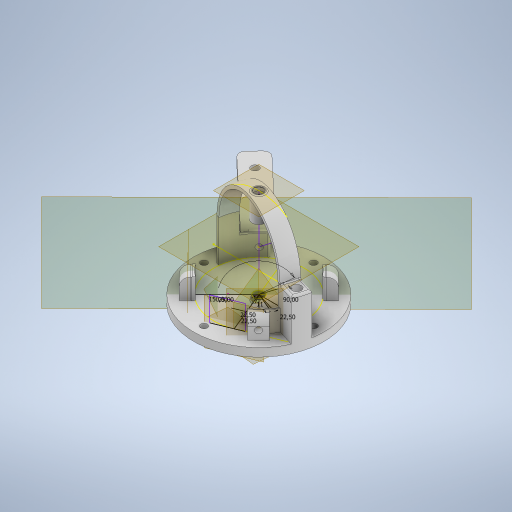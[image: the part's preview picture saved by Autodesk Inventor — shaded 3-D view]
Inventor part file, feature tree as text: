
AUTODESK INVENTOR PART (.ipt)
format: ipt  version: 2024 (Build 280153000, 153)  size: 738,816 bytes
history: native  units: in
note: dims shown in document units (in); Inventor stores cm internally (conversion verified against a paired STEP export)
features: sketch x38, extrude x19, plane x10, fillet x6, revolve x1, chamfer x1, pattern_circular x1
ambient origin geometry x8: Origin, YZ Plane, XZ Plane, XY Plane, X Axis, Y Axis, Z Axis, Center Point
bodies: Solid1 (feature_tree)
feature tree (76):
  extrude  "Plate"  Depth=0.1575in TaperAngle=0.0deg
  sketch  "Sketch4"  dims[d12=0.1969in d13=0.1299in]
  extrude  "Screw holes"  Depth=0.1299in
  extrude  "Optical hole"  Depth=0.1575in TaperAngle=0.0deg
  extrude  "Extrusion8"  Depth=0.1575in TaperAngle=0.0deg
  extrude  "Extrusion9"  Depth=0.3937in
  fillet  "Fillet1"  Radius=0.3937in
  sketch  "Sketch13"  dims[d60=0.1142in d61=7.874in d62=0.0in]
  plane  "Work Plane1"
  sketch  "Sketch15"  dims[d66=0.2362in d67=0.4724in]
  plane  "Work Plane2"
  extrude  "Extrusion12"  Depth=0.0394in
  extrude  "Extrusion13"  Depth=0.3937in TaperAngle=0.0deg
  fillet  "Fillet2"  Radius=0.0591in
  sketch  "Sketch29"  dims[d111=30.0deg]
  plane  "Work Plane5"
  sketch  "Sketch32"  dims[d120=0.3214in]
  plane  "Work Plane6"
  sketch  "Sketch36"  dims[d121=0.1732in d122=0.1181in d123=0.0in]
  sketch  "Sketch37"  dims[d124=0.1969in d125=0.0in d127=0.1575in]
  extrude  "Extrusion22"  Depth=7.874in TaperAngle=0.0deg
  extrude  "Extrusion23"  Depth=5.9055in TaperAngle=0.0deg
  extrude  "Extrusion24"  Depth=0.4724in
  sketch  "Sketch40"  dims[d134=0.7874in d135=90.0deg d136=0.1693in]
  sketch  "Sketch41"  dims[d137=0.2559in d138=0.3937in d139=0.0in]
  plane  "Work Plane7"
  sketch  "Sketch42"  dims[d140=0.2559in d141=0.1811in]
  revolve  "Revolution3"  [1 undecoded]
  sketch  "Sketch43"  dims[d142=0.4724in d143=0.0in d144=0.0394in d145=0.0394in]
  sketch  "Sketch44"  dims[d146=0.0197in d147=0.0787in d148=45.0deg d149=0.1181in d150=0.0394in d151=0.0in d152=0.0in]
  plane  "Work Plane8"
  extrude  "Extrusion25"  Depth=0.3937in
  extrude  "Extrusion26"  Depth=0.1575in
  fillet  "Fillet6"  Radius=1.7323in
  fillet  "Fillet7"  [1 undecoded]
  chamfer  "Chamfer1"  Distance=0.1181in
  extrude  "Extrusion27"  Depth=0.1575in
  pattern_circular  "Circular Pattern1"  Count=2  [1 undecoded]
  extrude  "Extrusion11"  TaperAngle=90.0deg  [1 undecoded]
  extrude  "Extrusion10"  TaperAngle=90.0deg  [1 undecoded]
  fillet  "Fillet8"  Radius=0.1693in
  sketch  "Sketch48"  dims[d158=22.5deg]
  sketch  "Sketch50"  dims[d159=0.4331in]
  sketch  "Sketch51"  dims[d162=22.5deg]
  plane  "Work Plane10"
  sketch  "Sketch52"  dims[d163=22.5deg]
  sketch  "Sketch55"  dims[d164=0.1772in]
  plane  "Work Plane12"
  sketch  "Sketch56"  dims[d165=0.7087in d166=0.0in]
  plane  "Work Plane13"
  extrude  "Extrusion28"  Depth=0.3937in TaperAngle=0.0deg
  plane  "Work Plane14"
  sketch  "Sketch58"  dims[d169=0.3937in d170=0.0in]
  extrude  "Extrusion29"  Depth=0.1811in
  sketch  "Sketch61"
  extrude  "Extrusion30"  Depth=0.0394in
  fillet  "Fillet9"  Radius=0.0394in
  sketch  "Sketch1"  dims[d0=2.4803in d1=0.1575in d2=0.0in]
  sketch  "Sketch5"  dims[d14=1.5748in d16=360.0deg d18=0.1575in d19=0.0in]
  sketch  "Sketch8"  dims[d34=0.1969in d35=0.1575in d36=0.0in]
  sketch  "Sketch11"  dims[d51=45.0deg d52=0.0394in]
  sketch  "Sketch12"  dims[d53=1.5748in d55=360.0deg d57=0.3937in d58=0.0in d59=0.0591in]
  sketch  "Sketch14"  dims[d63=0.1142in d64=5.9055in d65=0.0in]
  sketch  "Sketch16"  dims[d68=2.3622in d69=0.1575in d70=0.0in]
  sketch  "Sketch17"  dims[d72=0.3937in d73=0.1437in]
  sketch  "Sketch18"  dims[d74=0.1575in d75=0.0in d76=0.1181in d78=1.7323in d108=90.0deg]
  sketch  "Sketch38"  dims[d128=0.315in d129=0.7874in d130=0.0in]
  sketch  "Sketch39"  dims[d131=0.3937in d132=0.0in d133=90.0deg]
  sketch  "Sketch45"  dims[d153=1.5748in d154=360.0deg]
  sketch  "Sketch46"  dims[d156=0.1575in]
  sketch  "Sketch47"  dims[d157=0.1718in]
  sketch  "Sketch57"  dims[d167=0.7087in d168=0.0in]
  sketch  "Sketch60"  dims[d171=0.0394in]
  sketch  "Sketch62"
  sketch  "Sketch10"  dims[d39=1.5748in d40=360.0deg d41=0.4882in d42=0.2638in d43=45.0deg d45=0.0in d46=0.0394in d48=1.8504in d49=0.3937in d50=0.0in]
  extrude  "Extrusion7"  Depth=0.0394in TaperAngle=0.0deg
note: 5 required parameter values undecoded (feature->parameter linkage not recoverable at this tier; creation-order binding heuristic only, values carry confidence <= 0.55)